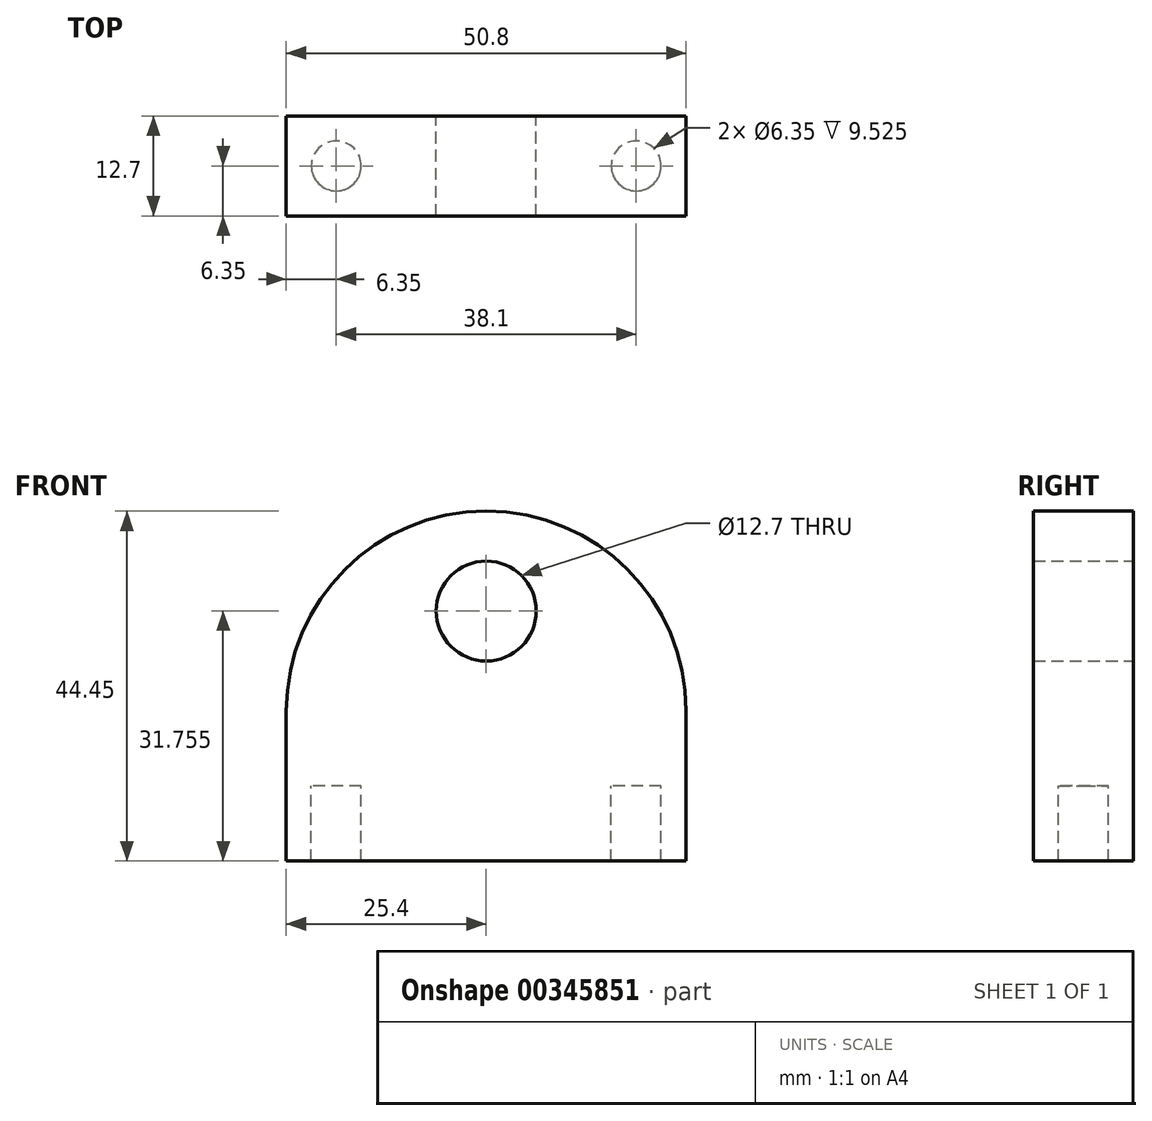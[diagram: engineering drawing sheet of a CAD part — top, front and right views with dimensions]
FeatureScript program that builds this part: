
annotation { "Feature Type Name" : "Feature", "Feature Type Description" : "" }
export const myFeature = defineFeature(function(context is Context, id is Id, definition is map)
    precondition{}
    {
        {
            var Q0;
            Q0=qCreatedBy(makeId("Front.planeOp"),FACE);
            var sketch = newSketch(context, id + "F2", { "sketchPlane" : qUnion([Q0])});
            skLineSegment(sketch, "E0.bottom", {"start": v(25.4, -9.52) * mm, "end": v(-25.4, -9.52) * mm});
            skLineSegment(sketch, "E0.top", {"start": v(-25.4, 9.53) * mm, "end": v(-25.4, 9.53) * mm});
            skLineSegment(sketch, "E0.left", {"start": v(25.4, -9.52) * mm, "end": v(25.4, 9.53) * mm});
            skLineSegment(sketch, "E0.right", {"start": v(-25.4, -9.52) * mm, "end": v(-25.4, 9.53) * mm});
            skPoint(sketch, "E0.middle", {"position": v(0, 0) * mm});
            skArc(sketch, "E1", {"start": v(25.4, 9.53) * mm, "mid": v(0, 34.93) * mm, "end": v(-25.4, 9.53) * mm});
            skCircle(sketch, "E2", {"center": v(0, 22.23) * mm, "radius": 6.35 * mm});
            skPoint(sketch, "E3.positionSnap0", {"position": v(0, -9.52) * mm});
            skSolve(sketch);
        }
        {
            var Q0;
            Q0=makeQuery(id+"F2.imprint","IMPRINT",FACE,{"disambiguationData":[TD([[makeQuery(id+"F2.imprint","IMPRINT",EDGE,{"derivedFrom":sQuery(id+"F2.wireOp",EDGE,"E0.bottom")}),-1.0]])]});
            extrude(context, id + "F0", {"entities" : qUnion([Q0]), "depth" : 12.7 * mm});
        }
        {
            var Q0;
            Q0=qCreatedBy(makeId("Top.planeOp"),FACE);
            var sketch = newSketch(context, id + "F3", { "sketchPlane" : qUnion([Q0])});
            skPoint(sketch, "E4", {"position": v(-19.05, 0) * mm});
            skPoint(sketch, "E5", {"position": v(19.05, 0) * mm});
            skPoint(sketch, "E6", {"position": v(-19.05, -6.35) * mm});
            skPoint(sketch, "E7", {"position": v(19.05, -6.35) * mm});
            skSolve(sketch);
        }
        {
            var Q0;
            Q0=sQuery(id+"F3.wireOp",VERTEX,"E7");
            var Q1;
            Q1=sQuery(id+"F3.wireOp",VERTEX,"E6");
            var Q2;
            Q2=makeQuery(id+"F0.opExtrude","SWEPT_BODY",BODY,{"disambiguationData":[OSD([sQuery(id+"F2.wireOp",EDGE,"E0.bottom"),sQuery(id+"F2.wireOp",EDGE,"E0.left"),sQuery(id+"F2.wireOp",EDGE,"E0.right"),sQuery(id+"F2.wireOp",EDGE,"E1"),sQuery(id+"F2.wireOp",EDGE,"E2")])]});
            hole(context, id + "F1", {"style" : HoleStyle.SIMPLE, "endStyle" : HoleEndStyle.BLIND, "holeDiameter" : 6.35 * mm, "holeDepth" : 19.05 * mm, "locations" : qUnion([Q0, Q1]), "scope" : qUnion([Q2])});
        }
    });
